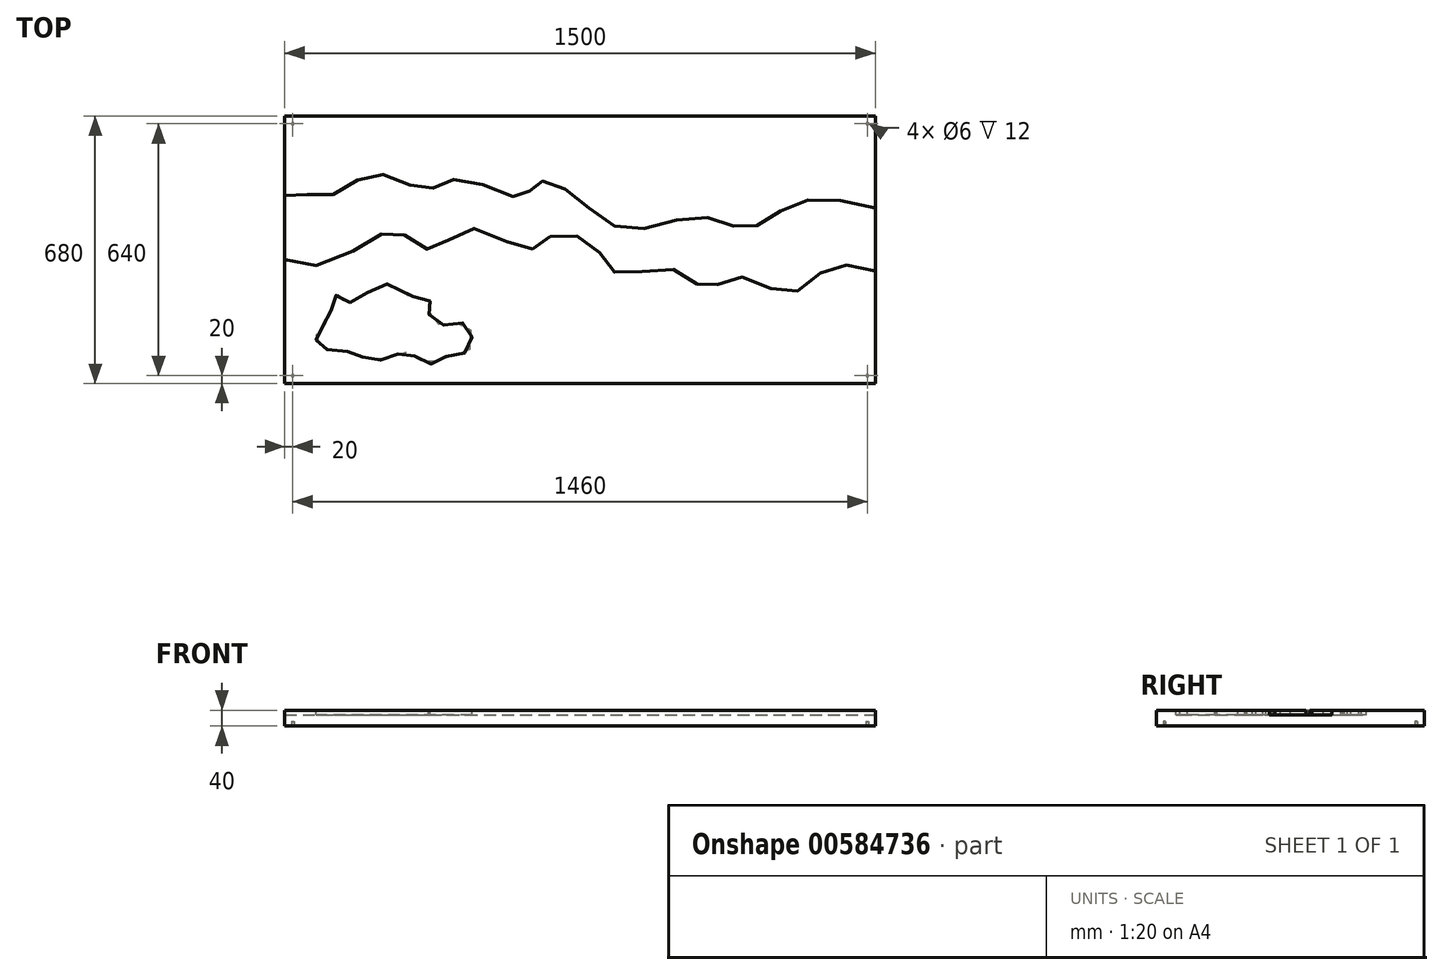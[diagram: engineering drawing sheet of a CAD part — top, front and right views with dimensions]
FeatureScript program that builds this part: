
annotation { "Feature Type Name" : "Feature", "Feature Type Description" : "" }
export const myFeature = defineFeature(function(context is Context, id is Id, definition is map)
    precondition{}
    {
        {
            var Q0;
            Q0=qCreatedBy(makeId("Top.planeOp"),FACE);
            var sketch = newSketch(context, id + "F0", { "sketchPlane" : qUnion([Q0])});
            skLineSegment(sketch, "E0.bottom", {"start": v(0, 0) * mm, "end": v(-1500, 0) * mm});
            skLineSegment(sketch, "E0.top", {"start": v(0, 680) * mm, "end": v(-1500, 680) * mm});
            skLineSegment(sketch, "E0.left", {"start": v(0, 0) * mm, "end": v(0, 680) * mm});
            skLineSegment(sketch, "E0.right", {"start": v(-1500, 0) * mm, "end": v(-1500, 680) * mm});
            skSolve(sketch);
        }
        {
            var Q0;
            Q0=makeQuery(id+"F0.imprint","IMPRINT",FACE,{"disambiguationData":[TD([[makeQuery(id+"F0.imprint","IMPRINT",EDGE,{"derivedFrom":sQuery(id+"F0.wireOp",EDGE,"E0.bottom")}),-1.0]])]});
            extrude(context, id + "F1", {"entities" : qUnion([Q0]), "depth" : 40 * mm, "offsetDistance" : 25 * mm});
        }
        {
            var Q0;
            Q0=makeQuery(id+"F1.opExtrude","CAP_FACE",FACE,{"disambiguationData":[OSD([sQuery(id+"F0.wireOp",EDGE,"E0.bottom"),sQuery(id+"F0.wireOp",EDGE,"E0.top"),sQuery(id+"F0.wireOp",EDGE,"E0.left"),sQuery(id+"F0.wireOp",EDGE,"E0.right")])],"isStart":true});
            var sketch = newSketch(context, id + "F2", { "sketchPlane" : qUnion([Q0])});
            skCircle(sketch, "E1", {"center": v(-1480, -20) * mm, "radius": 3 * mm});
            skSolve(sketch);
        }
        {
            var Q0;
            Q0=makeQuery(id+"F2.imprint","IMPRINT",FACE,{"disambiguationData":[TD([[makeQuery(id+"F2.imprint","IMPRINT",EDGE,{"derivedFrom":sQuery(id+"F2.wireOp",EDGE,"E1")}),1.0]])]});
            var Q1;
            Q1=sQuery(id+"F2.wireOp",EDGE,"E1");
            extrude(context, id + "F3", {"entities" : qUnion([Q0]), "operationType" : NewBodyOperationType.REMOVE, "surfaceEntities" : qUnion([Q1]), "oppositeDirection" : true, "depth" : 12 * mm, "offsetDistance" : 25 * mm});
        }
        {
            var Q0;
            Q0=makeQuery(id+"F1.opExtrude","CAP_FACE",FACE,{"disambiguationData":[OSD([sQuery(id+"F0.wireOp",EDGE,"E0.bottom"),sQuery(id+"F0.wireOp",EDGE,"E0.top"),sQuery(id+"F0.wireOp",EDGE,"E0.left"),sQuery(id+"F0.wireOp",EDGE,"E0.right")])],"isStart":false});
            var sketch = newSketch(context, id + "F4", { "sketchPlane" : qUnion([Q0])});
            skPoint(sketch, "E2.14.internal.snap0", {"position": v(-1500, 340) * mm});
            skPoint(sketch, "E2.16.internal.snap0", {"position": v(-1500, 340) * mm});
            skPoint(sketch, "E2.18.internal.snap0", {"position": v(-1500, 340) * mm});
            skFitSpline(sketch, "E2", {"points": [v(0, 445.32) * mm, v(-198.85, 459.55) * mm, v(-320.88, 395.06) * mm, v(-446.87, 423.96) * mm, v(-634.18, 391.54) * mm, v(-774.45, 485.82) * mm, v(-861.71, 509.2) * mm, v(-897.48, 473.43) * mm, v(-1054.2, 520.28) * mm, v(-1142.67, 493.77) * mm, v(-1271.47, 533.14) * mm, v(-1395.36, 475.63) * mm, v(-1500, 477.63) * mm, v(-1500, 315.3) * mm, v(-1321.48, 340) * mm, v(-1211.86, 385.08) * mm, v(-1126.58, 340) * mm, v(-1031.56, 394.07) * mm, v(-883.39, 340) * mm, v(-825.12, 373.5) * mm, v(-717.74, 353.1) * mm, v(-656.9, 280.32) * mm, v(-517.97, 291.46) * mm, v(-430.62, 244.1) * mm, v(-345.48, 270.7) * mm, v(-218.35, 229.5) * mm, v(-118.4, 292.84) * mm, v(0, 286.5) * mm], "startDerivative": vector(-4535.7, 1100.87) * mm, "endDerivative": vector(3438.34, -939.7) * mm});
            skFitSpline(sketch, "E3", {"points": [v(0, 286.5) * mm, v(0, 445.32) * mm], "startDerivative": vector(0, 158.83) * mm, "endDerivative": vector(0, 158.83) * mm});
            skFitSpline(sketch, "E4", {"points": [v(-1500, 315.3) * mm, v(-1500, 477.63) * mm], "startDerivative": vector(0, 162.33) * mm, "endDerivative": vector(0, 162.33) * mm});
            skFitSpline(sketch, "E5", {"points": [v(-1525.04, 391.54) * mm, v(-1525.05, 402.86) * mm], "startDerivative": vector(0.11, 11.32) * mm, "endDerivative": vector(0.11, 11.32) * mm});
            skPoint(sketch, "E6.14.internal.snap0", {"position": v(-311.95, -26.99) * mm});
            skPoint(sketch, "E6.16.internal.snap0", {"position": v(-311.95, -26.99) * mm});
            skPoint(sketch, "E6.18.internal.snap0", {"position": v(-311.95, -26.99) * mm});
            skFitSpline(sketch, "E6", {"points": [v(1188.05, 78.34) * mm, v(989.2, 92.57) * mm, v(867.17, 28.07) * mm, v(741.18, 56.97) * mm, v(553.87, 24.55) * mm, v(413.6, 118.83) * mm, v(326.34, 142.21) * mm, v(290.57, 106.44) * mm, v(133.85, 153.3) * mm, v(45.38, 126.78) * mm, v(-83.42, 166.16) * mm, v(-207.31, 108.64) * mm, v(-311.95, 110.65) * mm, v(-311.95, -51.68) * mm, v(-133.43, -26.99) * mm, v(-23.8, 18.1) * mm, v(61.47, -26.99) * mm, v(156.5, 27.08) * mm, v(304.66, -26.99) * mm, v(362.92, 6.52) * mm, v(470.3, -13.9) * mm, v(531.14, -86.66) * mm, v(670.08, -75.53) * mm, v(757.43, -122.88) * mm, v(842.56, -96.3) * mm, v(969.7, -137.5) * mm, v(1069.64, -74.14) * mm, v(1188.05, -80.5) * mm], "startDerivative": vector(-4535.7, 1100.87) * mm, "endDerivative": vector(3438.34, -939.7) * mm});
            skFitSpline(sketch, "E7", {"points": [v(1188.05, -80.5) * mm, v(1188.05, 78.34) * mm], "startDerivative": vector(0, 158.83) * mm, "endDerivative": vector(0, 158.83) * mm});
            skFitSpline(sketch, "E8", {"points": [v(-311.95, -51.68) * mm, v(-311.95, 110.65) * mm], "startDerivative": vector(0, 162.33) * mm, "endDerivative": vector(0, 162.33) * mm});
            skFitSpline(sketch, "E9", {"points": [v(-337, 24.55) * mm, v(-337, 35.88) * mm], "startDerivative": vector(0.11, 11.32) * mm, "endDerivative": vector(0.11, 11.32) * mm});
            skSolve(sketch);
        }
        {
            var Q0;
            {var subQ0=sQuery(id+"F4.wireOp",EDGE,"E3");Q0=makeQuery(id+"F4.imprint","IMPRINT",FACE,{"disambiguationData":[TD([[makeQuery(id+"F4.imprint","IMPRINT",EDGE,{"derivedFrom":subQ0}),1.0]])]});}
            extrude(context, id + "F5", {"entities" : qUnion([Q0]), "operationType" : NewBodyOperationType.REMOVE, "oppositeDirection" : true, "depth" : 12 * mm, "offsetDistance" : 25 * mm});
        }
        {
            var Q0;
            {var subQ0=sQuery(id+"F0.wireOp",EDGE,"E0.bottom");var subQ1=sQuery(id+"F0.wireOp",EDGE,"E0.right");var subQ3=sQuery(id+"F0.wireOp",EDGE,"E0.left");Q0=makeQuery(id+"F5.boolean.opBoolean","SPLIT",FACE,{"disambiguationData":[TD([makeQuery(id+"F1.opExtrude","SWEPT_FACE",FACE,{"disambiguationData":[OSD([subQ0])]})])],"derivedFrom":makeQuery(id+"F1.opExtrude","CAP_FACE",FACE,{"disambiguationData":[OSD([subQ0,sQuery(id+"F0.wireOp",EDGE,"E0.top"),subQ3,subQ1])],"isStart":false})});}
            var sketch = newSketch(context, id + "F6", { "sketchPlane" : qUnion([Q0])});
            skFitSpline(sketch, "E10", {"points": [v(-1334.77, 206.48) * mm, v(-1264.77, 247.33) * mm, v(-1214.95, 245.43) * mm, v(-1193.53, 225.15) * mm, v(-1132.42, 211.38) * mm, v(-1135.15, 181.72) * mm, v(-1094.67, 148.12) * mm, v(-1037.19, 150.51) * mm, v(-1031.48, 85.04) * mm, v(-1086.5, 69.96) * mm, v(-1132.57, 49.96) * mm, v(-1189.55, 78.46) * mm, v(-1242.33, 62.15) * mm, v(-1302.16, 66.71) * mm, v(-1345.6, 82.1) * mm, v(-1413.32, 93.84) * mm, v(-1415.17, 131.7) * mm, v(-1387.1, 167.26) * mm, v(-1371.62, 223.91) * mm, v(-1334.77, 206.48) * mm]});
            skSolve(sketch);
        }
        {
            var Q0;
            Q0=makeQuery(id+"F6.imprint","IMPRINT",FACE,{"disambiguationData":[TD([[makeQuery(id+"F6.imprint","IMPRINT",EDGE,{"derivedFrom":sQuery(id+"F6.wireOp",EDGE,"E10")}),-1.0]])]});
            extrude(context, id + "F7", {"entities" : qUnion([Q0]), "operationType" : NewBodyOperationType.REMOVE, "oppositeDirection" : true, "depth" : 12 * mm, "offsetDistance" : 25 * mm});
        }
        {
            var Q0;
            Q0=makeQuery(id+"F1.opExtrude","CAP_FACE",FACE,{"disambiguationData":[OSD([sQuery(id+"F0.wireOp",EDGE,"E0.bottom"),sQuery(id+"F0.wireOp",EDGE,"E0.top"),sQuery(id+"F0.wireOp",EDGE,"E0.left"),sQuery(id+"F0.wireOp",EDGE,"E0.right")])],"isStart":true});
            var sketch = newSketch(context, id + "F8", { "sketchPlane" : qUnion([Q0])});
            skCircle(sketch, "E11", {"center": v(-1480, -660) * mm, "radius": 3 * mm});
            skCircle(sketch, "E12", {"center": v(-20, -660) * mm, "radius": 3 * mm});
            skCircle(sketch, "E13", {"center": v(-20, -20) * mm, "radius": 3 * mm});
            skSolve(sketch);
        }
        {
            var Q0;
            Q0=makeQuery(id+"F8.imprint","IMPRINT",FACE,{"disambiguationData":[TD([[makeQuery(id+"F8.imprint","IMPRINT",EDGE,{"derivedFrom":sQuery(id+"F8.wireOp",EDGE,"E11")}),1.0]])]});
            var Q1;
            Q1=makeQuery(id+"F8.imprint","IMPRINT",FACE,{"disambiguationData":[TD([[makeQuery(id+"F8.imprint","IMPRINT",EDGE,{"derivedFrom":sQuery(id+"F8.wireOp",EDGE,"E12")}),1.0]])]});
            var Q2;
            Q2=makeQuery(id+"F8.imprint","IMPRINT",FACE,{"disambiguationData":[TD([[makeQuery(id+"F8.imprint","IMPRINT",EDGE,{"derivedFrom":sQuery(id+"F8.wireOp",EDGE,"E13")}),1.0]])]});
            extrude(context, id + "F9", {"entities" : qUnion([Q0, Q1, Q2]), "operationType" : NewBodyOperationType.REMOVE, "oppositeDirection" : true, "depth" : 12 * mm, "offsetDistance" : 25 * mm});
        }
    });
